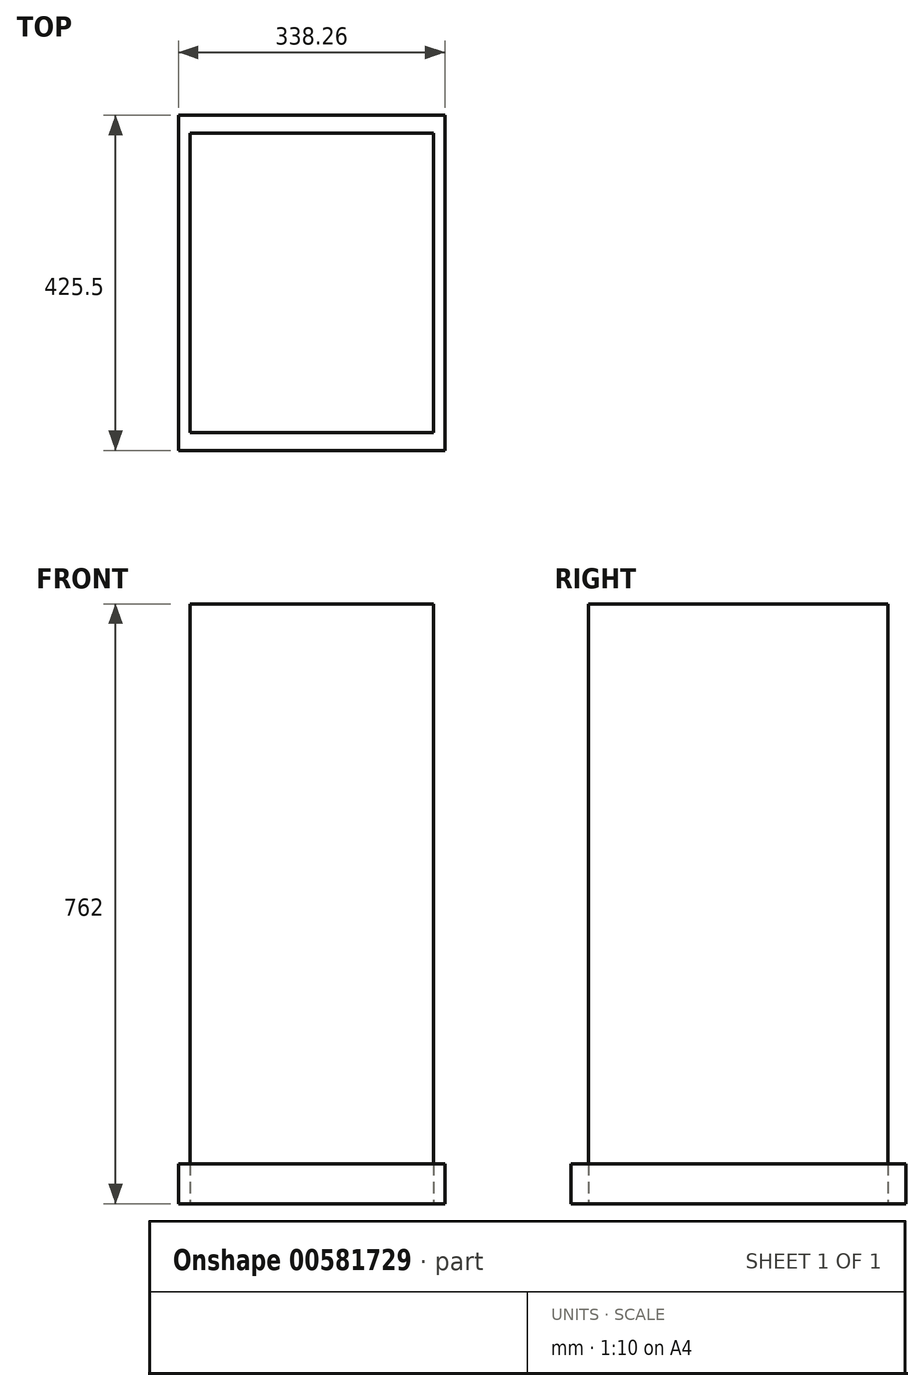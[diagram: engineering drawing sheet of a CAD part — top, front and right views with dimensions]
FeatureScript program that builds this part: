
annotation { "Feature Type Name" : "Feature", "Feature Type Description" : "" }
export const myFeature = defineFeature(function(context is Context, id is Id, definition is map)
    precondition{}
    {
        {
            var Q0;
            Q0=qCreatedBy(makeId("Top.planeOp"),FACE);
            var sketch = newSketch(context, id + "F0", { "sketchPlane" : qUnion([Q0])});
            skLineSegment(sketch, "E0.bottom", {"start": v(169.13, -212.75) * mm, "end": v(-169.13, -212.75) * mm});
            skLineSegment(sketch, "E0.top", {"start": v(169.13, 212.75) * mm, "end": v(-169.13, 212.75) * mm});
            skLineSegment(sketch, "E0.left", {"start": v(169.13, -212.75) * mm, "end": v(169.13, 212.75) * mm});
            skLineSegment(sketch, "E0.right", {"start": v(-169.13, -212.75) * mm, "end": v(-169.13, 212.75) * mm});
            skPoint(sketch, "E0.middle", {"position": v(0, 0) * mm});
            skLineSegment(sketch, "E1.bottom", {"start": v(154.69, -190.2) * mm, "end": v(-154.69, -190.2) * mm});
            skLineSegment(sketch, "E1.top", {"start": v(154.69, 190.2) * mm, "end": v(-154.69, 190.2) * mm});
            skLineSegment(sketch, "E1.left", {"start": v(154.69, -190.2) * mm, "end": v(154.69, 190.2) * mm});
            skLineSegment(sketch, "E1.right", {"start": v(-154.69, -190.2) * mm, "end": v(-154.69, 190.2) * mm});
            skSolve(sketch);
        }
        {
            var Q0;
            Q0=makeQuery(id+"F0.imprint","IMPRINT",FACE,{"disambiguationData":[TD([[makeQuery(id+"F0.imprint","IMPRINT",EDGE,{"derivedFrom":sQuery(id+"F0.wireOp",EDGE,"E0.bottom")}),-1.0]])]});
            extrude(context, id + "F1", {"entities" : qUnion([Q0]), "depth" : 50.8 * mm, "offsetDistance" : 25.4 * mm});
        }
        {
            var Q0;
            Q0=makeQuery(id+"F1.opExtrude","CAP_FACE",FACE,{"disambiguationData":[OSD([sQuery(id+"F0.wireOp",EDGE,"E0.bottom"),sQuery(id+"F0.wireOp",EDGE,"E0.top"),sQuery(id+"F0.wireOp",EDGE,"E0.left"),sQuery(id+"F0.wireOp",EDGE,"E0.right"),sQuery(id+"F0.wireOp",EDGE,"E1.bottom"),sQuery(id+"F0.wireOp",EDGE,"E1.top"),sQuery(id+"F0.wireOp",EDGE,"E1.left"),sQuery(id+"F0.wireOp",EDGE,"E1.right")])],"isStart":false});
            var sketch = newSketch(context, id + "F2", { "sketchPlane" : qUnion([Q0])});
            skLineSegment(sketch, "E2.bottom", {"start": v(154.69, 190.2) * mm, "end": v(-154.69, 190.2) * mm});
            skLineSegment(sketch, "E2.top", {"start": v(154.69, -190.2) * mm, "end": v(-154.69, -190.2) * mm});
            skLineSegment(sketch, "E2.left", {"start": v(154.69, 190.2) * mm, "end": v(154.69, -190.2) * mm});
            skLineSegment(sketch, "E2.right", {"start": v(-154.69, 190.2) * mm, "end": v(-154.69, -190.2) * mm});
            skSolve(sketch);
        }
        {
            var Q0;
            Q0=makeQuery(id+"F2.imprint","IMPRINT",FACE,{"disambiguationData":[TD([[makeQuery(id+"F2.imprint","IMPRINT",EDGE,{"derivedFrom":sQuery(id+"F2.wireOp",EDGE,"E2.bottom")}),1.0]])]});
            extrude(context, id + "F3", {"entities" : qUnion([Q0]), "depth" : 711.2 * mm, "offsetDistance" : 25.4 * mm});
        }
    });
